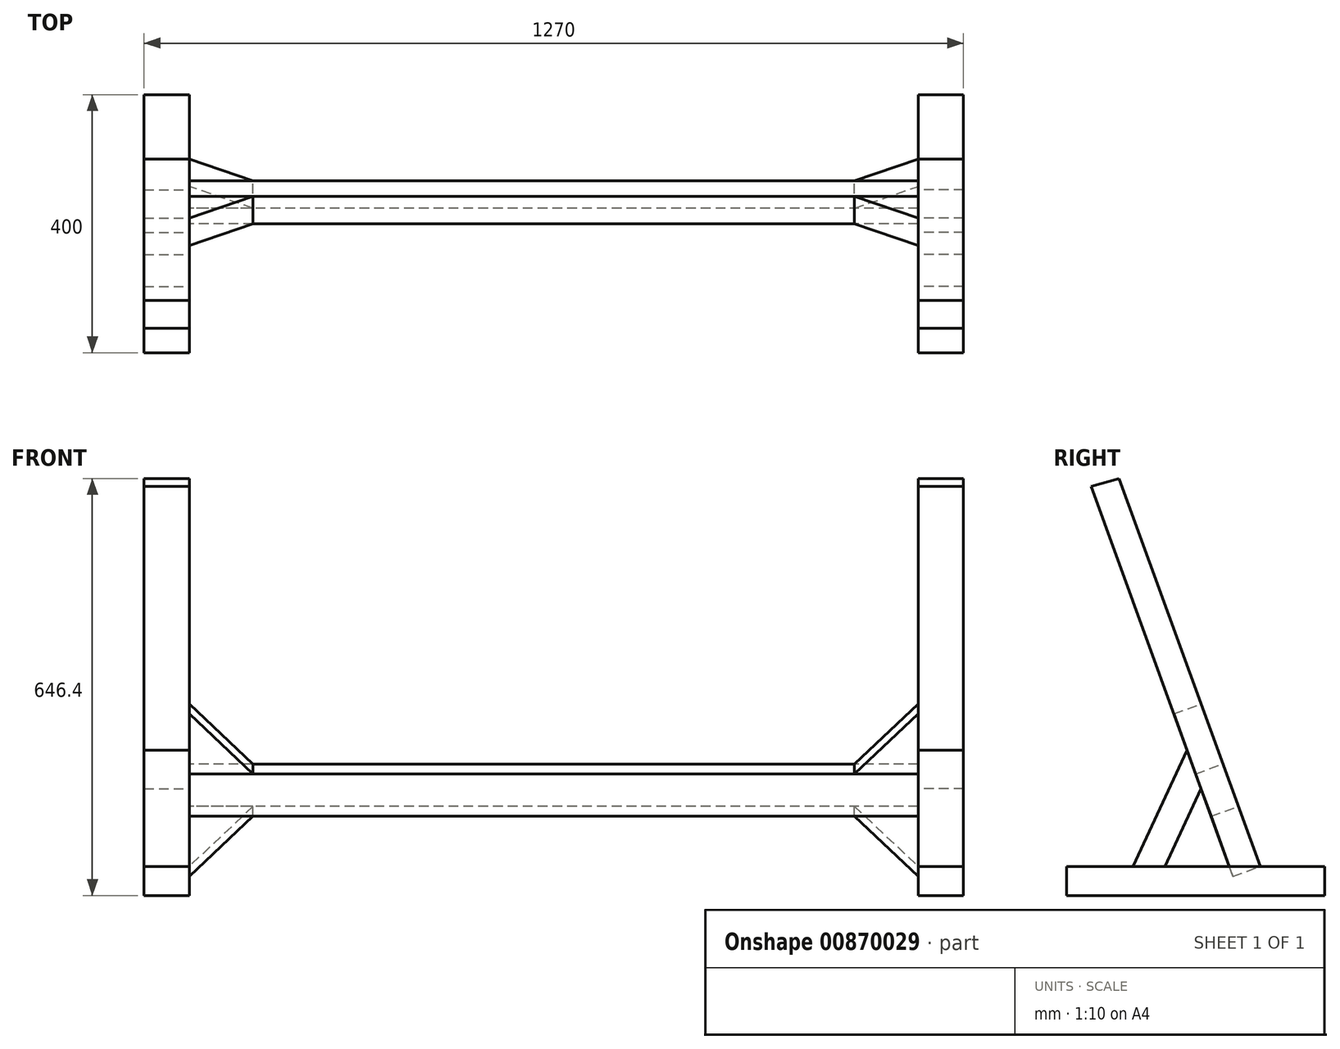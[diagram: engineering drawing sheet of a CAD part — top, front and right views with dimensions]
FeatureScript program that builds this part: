
annotation { "Feature Type Name" : "Feature", "Feature Type Description" : "" }
export const myFeature = defineFeature(function(context is Context, id is Id, definition is map)
    precondition{}
    {
        {
            var Q0;
            Q0=qCreatedBy(makeId("Right.planeOp"),FACE);
            var sketch = newSketch(context, id + "F0", { "sketchPlane" : qUnion([Q0])});
            skLineSegment(sketch, "E0.bottom", {"start": v(0, 0) * mm, "end": v(-400, 0) * mm});
            skLineSegment(sketch, "E0.top", {"start": v(0, 45) * mm, "end": v(-400, 45) * mm});
            skLineSegment(sketch, "E0.left", {"start": v(0, 0) * mm, "end": v(0, 45) * mm});
            skLineSegment(sketch, "E0.right", {"start": v(-400, 0) * mm, "end": v(-400, 45) * mm});
            skLineSegment(sketch, "E1", {"start": v(-100, 45) * mm, "end": v(-318.9, 646.4) * mm});
            skLineSegment(sketch, "E2", {"start": v(-318.9, 646.4) * mm, "end": v(-318.9, 646.4) * mm});
            skLineSegment(sketch, "E3", {"start": v(-318.9, 646.4) * mm, "end": v(-362.1, 633.85) * mm});
            skLineSegment(sketch, "E4", {"start": v(-362.1, 633.85) * mm, "end": v(-147.78, 45) * mm});
            skLineSegment(sketch, "E5", {"start": v(-213.39, 225.24) * mm, "end": v(-297.43, 45) * mm});
            skLineSegment(sketch, "E6", {"start": v(-191.62, 165.44) * mm, "end": v(-247.78, 45) * mm});
            skSolve(sketch);
        }
        {
            var Q0;
            Q0=makeQuery(id+"F0.imprint","IMPRINT",FACE,{"disambiguationData":[TD([[makeQuery(id+"F0.imprint","IMPRINT",EDGE,{"derivedFrom":sQuery(id+"F0.wireOp",EDGE,"E0.bottom")}),-1.0]])]});
            extrude(context, id + "F1", {"entities" : qUnion([Q0]), "depth" : 70 * mm, "offsetDistance" : 25 * mm});
        }
        {
            var Q0;
            {var subQ0=sQuery(id+"F0.wireOp",EDGE,"E5");Q0=makeQuery(id+"F0.imprint","IMPRINT",FACE,{"disambiguationData":[TD([[makeQuery(id+"F0.imprint","IMPRINT",EDGE,{"derivedFrom":subQ0}),1.0]])]});}
            extrude(context, id + "F2", {"entities" : qUnion([Q0]), "depth" : 70 * mm, "offsetDistance" : 25 * mm});
        }
        {
            var Q0;
            {var subQ3=sQuery(id+"F0.wireOp",EDGE,"E1");Q0=makeQuery(id+"F0.imprint","IMPRINT",FACE,{"disambiguationData":[TD([[makeQuery(id+"F0.imprint","IMPRINT",EDGE,{"derivedFrom":subQ3}),1.0]])]});}
            extrude(context, id + "F3", {"entities" : qUnion([Q0]), "depth" : 70 * mm, "offsetDistance" : 25 * mm});
        }
        {
            var Q0;
            Q0=makeQuery(id+"F1.opExtrude","SWEPT_BODY",BODY,{"disambiguationData":[OSD([sQuery(id+"F0.wireOp",EDGE,"E0.bottom"),sQuery(id+"F0.wireOp",EDGE,"E0.top"),sQuery(id+"F0.wireOp",EDGE,"E0.left"),sQuery(id+"F0.wireOp",EDGE,"E0.right")])]});
            var Q1;
            Q1=makeQuery(id+"F2.opExtrude","SWEPT_BODY",BODY,{"disambiguationData":[OSD([sQuery(id+"F0.wireOp",EDGE,"E0.top"),sQuery(id+"F0.wireOp",EDGE,"E4"),sQuery(id+"F0.wireOp",EDGE,"E5"),sQuery(id+"F0.wireOp",EDGE,"E6")])]});
            var Q2;
            Q2=makeQuery(id+"F3.opExtrude","SWEPT_BODY",BODY,{"disambiguationData":[OSD([sQuery(id+"F0.wireOp",EDGE,"E0.top"),sQuery(id+"F0.wireOp",EDGE,"E1"),sQuery(id+"F0.wireOp",EDGE,"E3"),sQuery(id+"F0.wireOp",EDGE,"E4")])]});
            var Q3;
            Q3=qCreatedBy(makeId("Right.planeOp"),FACE);
            mirror(context, id + "F4", {"entities" : qUnion([Q0, Q1, Q2]), "mirrorPlane" : qUnion([Q3])});
        }
        {
            var Q0;
            Q0=makeQuery(id+"F4.opPattern","COPY",BODY,{"derivedFrom":makeQuery(id+"F1.opExtrude","SWEPT_BODY",BODY,{"disambiguationData":[OSD([sQuery(id+"F0.wireOp",EDGE,"E0.bottom"),sQuery(id+"F0.wireOp",EDGE,"E0.top"),sQuery(id+"F0.wireOp",EDGE,"E0.left"),sQuery(id+"F0.wireOp",EDGE,"E0.right")])]}),"instanceName":"1"});
            var Q1;
            Q1=makeQuery(id+"F4.opPattern","COPY",BODY,{"derivedFrom":makeQuery(id+"F2.opExtrude","SWEPT_BODY",BODY,{"disambiguationData":[OSD([sQuery(id+"F0.wireOp",EDGE,"E0.top"),sQuery(id+"F0.wireOp",EDGE,"E4"),sQuery(id+"F0.wireOp",EDGE,"E5"),sQuery(id+"F0.wireOp",EDGE,"E6")])]}),"instanceName":"1"});
            var Q2;
            Q2=makeQuery(id+"F4.opPattern","COPY",BODY,{"derivedFrom":makeQuery(id+"F3.opExtrude","SWEPT_BODY",BODY,{"disambiguationData":[OSD([sQuery(id+"F0.wireOp",EDGE,"E0.top"),sQuery(id+"F0.wireOp",EDGE,"E1"),sQuery(id+"F0.wireOp",EDGE,"E3"),sQuery(id+"F0.wireOp",EDGE,"E4")])]}),"instanceName":"1"});
            var Q3;
            Q3=qCreatedBy(makeId("Right.planeOp"),FACE);
            transform(context, id + "F5", {"entities" : qUnion([Q0, Q1, Q2]), "transformType" : TransformType.TRANSLATION_DISTANCE, "transformDirection" : qUnion([Q3]), "distance" : 1130 * mm, "oppositeDirection" : true, "makeCopy" : false});
        }
        {
            var Q0;
            Q0=makeQuery(id+"F3.opExtrude","SWEPT_FACE",FACE,{"disambiguationData":[OSD([sQuery(id+"F0.wireOp",EDGE,"E1")])]});
            var sketch = newSketch(context, id + "F6", { "sketchPlane" : qUnion([Q0])});
            skLineSegment(sketch, "E7.right", {"start": v(1130, 716.49) * mm, "end": v(1130, 646.49) * mm});
            skLineSegment(sketch, "E8.bottom", {"start": v(0, 245.48) * mm, "end": v(1130, 245.48) * mm});
            skLineSegment(sketch, "E8.top", {"start": v(0, 175.48) * mm, "end": v(1130, 175.48) * mm});
            skLineSegment(sketch, "E8.left", {"start": v(0, 245.48) * mm, "end": v(0, 175.48) * mm});
            skLineSegment(sketch, "E8.right", {"start": v(1130, 245.48) * mm, "end": v(1130, 175.48) * mm});
            skLineSegment(sketch, "E9", {"start": v(99, 175.48) * mm, "end": v(0, 76.49) * mm});
            skLineSegment(sketch, "E10", {"start": v(1031, 175.48) * mm, "end": v(1130, 76.49) * mm});
            skLineSegment(sketch, "E11", {"start": v(1031, 245.48) * mm, "end": v(1130, 344.48) * mm});
            skLineSegment(sketch, "E12", {"start": v(99, 245.48) * mm, "end": v(0, 344.48) * mm});
            skLineSegment(sketch, "E13", {"start": v(1130, 175.48) * mm, "end": v(1130, 76.49) * mm});
            skLineSegment(sketch, "E14", {"start": v(1130, 245.48) * mm, "end": v(1130, 344.48) * mm});
            skSolve(sketch);
        }
        {
            var Q0;
            Q0=makeQuery(id+"F6.imprint","IMPRINT",FACE,{"disambiguationData":[TD([[makeQuery(id+"F6.imprint","IMPRINT",EDGE,{"derivedFrom":sQuery(id+"F6.wireOp",EDGE,"8MLd0JaE-k74V-EjUQ-NVDd-f5bv4FNSBLAQ.bottom")}),1.0]])]});
            var Q1;
            {var subQ0=sQuery(id+"F6.wireOp",EDGE,"E8.left");Q1=makeQuery(id+"F6.imprint","IMPRINT",FACE,{"disambiguationData":[TD([[makeQuery(id+"F6.imprint","IMPRINT",EDGE,{"derivedFrom":subQ0}),-1.0]])]});}
            extrude(context, id + "F7", {"entities" : qUnion([Q0, Q1]), "oppositeDirection" : true, "depth" : 45 * mm, "offsetDistance" : 25 * mm});
        }
        {
            var Q0;
            {var subQ3=sQuery(id+"F6.wireOp",EDGE,"E12");Q0=makeQuery(id+"F6.imprint","IMPRINT",FACE,{"disambiguationData":[TD([[makeQuery(id+"F6.imprint","IMPRINT",EDGE,{"derivedFrom":subQ3}),1.0]])]});}
            var Q1;
            {var subQ4=sQuery(id+"F6.wireOp",EDGE,"E9");Q1=makeQuery(id+"F6.imprint","IMPRINT",FACE,{"disambiguationData":[TD([[makeQuery(id+"F6.imprint","IMPRINT",EDGE,{"derivedFrom":subQ4}),-1.0]])]});}
            var Q2;
            {var subQ2=sQuery(id+"F6.wireOp",EDGE,"E10");Q2=makeQuery(id+"F6.imprint","IMPRINT",FACE,{"disambiguationData":[TD([[makeQuery(id+"F6.imprint","IMPRINT",EDGE,{"derivedFrom":subQ2}),1.0]])]});}
            var Q3;
            {var subQ2=sQuery(id+"F6.wireOp",EDGE,"E11");Q3=makeQuery(id+"F6.imprint","IMPRINT",FACE,{"disambiguationData":[TD([[makeQuery(id+"F6.imprint","IMPRINT",EDGE,{"derivedFrom":subQ2}),-1.0]])]});}
            extrude(context, id + "F8", {"entities" : qUnion([Q0, Q1, Q2, Q3]), "oppositeDirection" : true, "depth" : 45 * mm, "offsetDistance" : 25 * mm});
        }
    });
